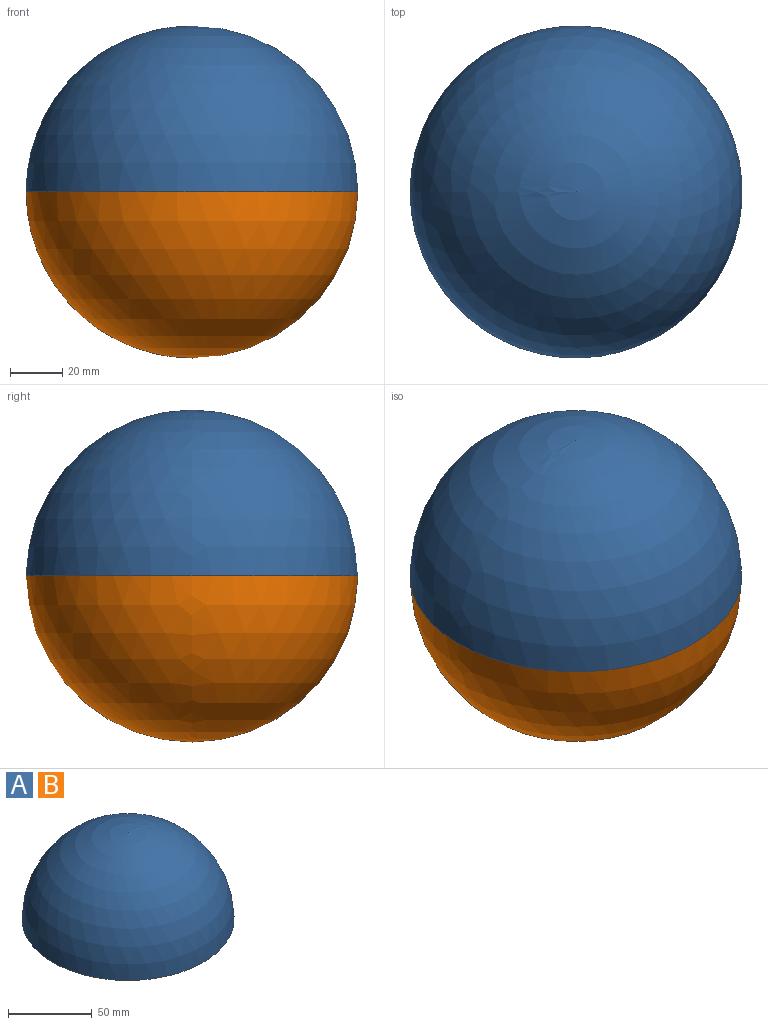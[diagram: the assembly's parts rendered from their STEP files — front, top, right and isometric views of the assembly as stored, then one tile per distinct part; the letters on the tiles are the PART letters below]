
ASSEMBLY  parts=2 mates=1
PART A: 2 faces, bbox 127x127x63.5 mm
  f0: plane 127x127mm, normal (0,0,-1), area 12667.7mm2, adj f1
  f1: sphere r=63.5mm, area 25335.4mm2, adj f0
PART B: same geometry as A
PLACE A rot(axis=(0,0,-1),180deg) t=(0,0,73.91)mm
PLACE B rot(axis=(0,-1,0),180deg) t=(0,0,73.91)mm
MATE fastened B.f0 <-> A.f0  axis (0,0,-1) through (0,0,73.91)mm
